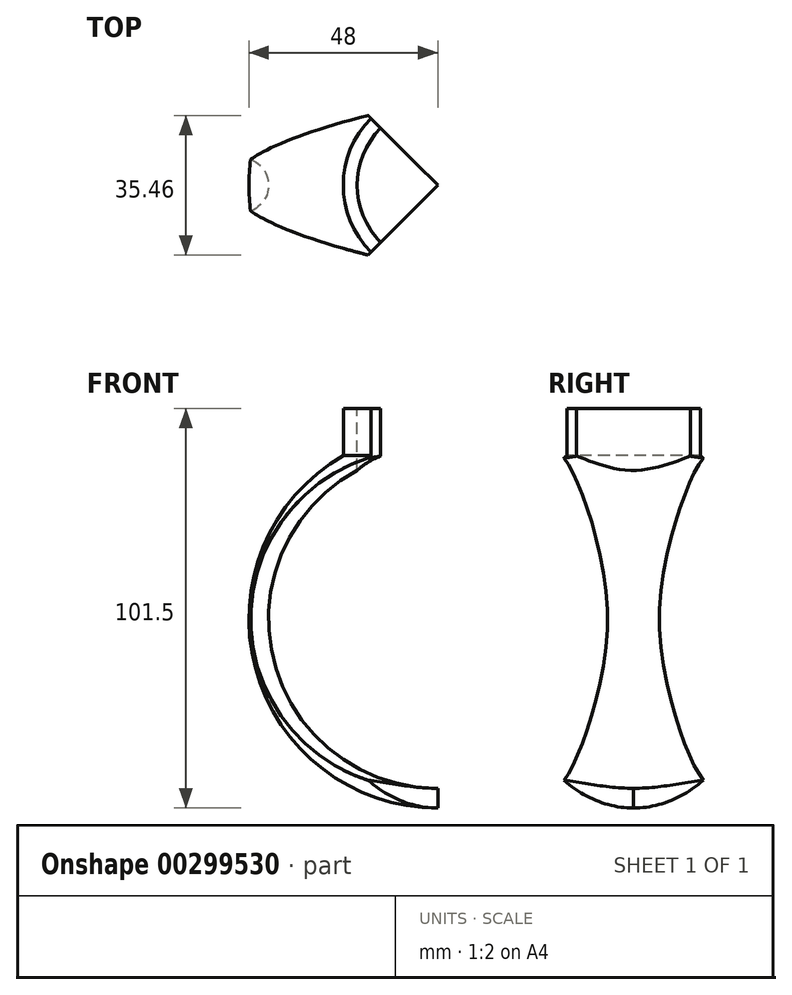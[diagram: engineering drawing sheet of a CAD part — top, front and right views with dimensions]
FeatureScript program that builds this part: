
annotation { "Feature Type Name" : "Feature", "Feature Type Description" : "" }
export const myFeature = defineFeature(function(context is Context, id is Id, definition is map)
    precondition{}
    {
        {
            var Q0;
            Q0=qCreatedBy(makeId("Front.planeOp"),FACE);
            var sketch = newSketch(context, id + "F0", { "sketchPlane" : qUnion([Q0])});
            skLineSegment(sketch, "E0.bottom", {"start": v(0, 75.1) * mm, "end": v(50, 75.1) * mm});
            skLineSegment(sketch, "E0.top", {"start": v(0, -75.3) * mm, "end": v(50, -75.3) * mm});
            skLineSegment(sketch, "E0.left", {"start": v(0, 75.1) * mm, "end": v(0, -75.3) * mm});
            skLineSegment(sketch, "E0.right", {"start": v(50, 75.1) * mm, "end": v(50, -75.3) * mm});
            skArc(sketch, "E1", {"start": v(50, 42.9) * mm, "mid": v(7, -0.1) * mm, "end": v(50, -43.1) * mm});
            skLineSegment(sketch, "E2", {"start": v(0, 53.4) * mm, "end": v(50, 53.4) * mm});
            skLineSegment(sketch, "E3", {"start": v(0, -50.35) * mm, "end": v(50, -50.35) * mm});
            skArc(sketch, "E4", {"start": v(26, 41.47) * mm, "mid": v(3.64, -12.52) * mm, "end": v(50, -48.1) * mm});
            skLineSegment(sketch, "E5", {"start": v(26, 53.4) * mm, "end": v(26, 41.47) * mm});
            skSolve(sketch);
        }
        {
            var Q0;
            {var subQ4=sQuery(id+"F0.wireOp",EDGE,"E1");Q0=makeQuery(id+"F0.imprint","IMPRINT",FACE,{"disambiguationData":[TD([[makeQuery(id+"F0.imprint","IMPRINT",EDGE,{"derivedFrom":subQ4}),-1.0]])]});}
            var Q1;
            Q1=sQuery(id+"F0.wireOp",EDGE,"E0.right");
            revolve(context, id + "F1", {"surfaceOperationType" : NewSurfaceOperationType.NEW, "entities" : qUnion([Q0]), "axis" : qUnion([Q1]), "revolveType" : RevolveType.SYMMETRIC, "angle" : 90 * degree});
        }
        {
            var Q0;
            {var subQ0=sQuery(id+"F0.wireOp",EDGE,"E1");Q0=makeQuery(id+"F0.imprint","IMPRINT",FACE,{"disambiguationData":[TD([[makeQuery(id+"F0.imprint","IMPRINT",EDGE,{"derivedFrom":subQ0}),1.0]])]});}
            var Q1;
            Q1=sQuery(id+"F0.wireOp",EDGE,"E0.left");
            revolve(context, id + "F2", {"operationType" : NewBodyOperationType.REMOVE, "surfaceOperationType" : NewSurfaceOperationType.NEW, "entities" : qUnion([Q0]), "axis" : qUnion([Q1]), "revolveType" : RevolveType.SYMMETRIC, "angle" : 180 * degree});
        }
        {
            var Q0;
            Q0=makeQuery(id+"F1.opRevolve","SWEPT_FACE",FACE,{"disambiguationData":[OSD([sQuery(id+"F0.wireOp",EDGE,"E2")])]});
            var sketch = newSketch(context, id + "F3", { "sketchPlane" : qUnion([Q0])});
            skCircle(sketch, "E6", {"center": v(50, 0) * mm, "radius": 20.5 * mm});
            skLineSegment(sketch, "E7.bottom", {"start": v(50, 0) * mm, "end": v(21.21, 28.79) * mm});
            skLineSegment(sketch, "E7.top", {"start": v(20.87, -29.13) * mm, "end": v(-7.92, -0.34) * mm});
            skLineSegment(sketch, "E7.left", {"start": v(50, 0) * mm, "end": v(20.87, -29.13) * mm});
            skLineSegment(sketch, "E7.right", {"start": v(21.21, 28.79) * mm, "end": v(-7.92, -0.34) * mm});
            skSolve(sketch);
        }
        {
            var Q0;
            {var subQ0=sQuery(id+"F3.wireOp",EDGE,"E6");var subQ1=sQuery(id+"F0.wireOp",EDGE,"E2");var subQ2=makeQuery(id+"F1.opRevolve","CAP_EDGE",EDGE,{"disambiguationData":[OSD([subQ1])],"isStart":true});var subQ3=makeQuery(id+"F3.imprint","INTERSECT",VERTEX,{"derivedFrom":[subQ2,subQ0]});Q0=makeQuery(id+"F3.imprint","IMPRINT",FACE,{"disambiguationData":[TD([[makeQuery(id+"F3.imprint","IMPRINT",EDGE,{"disambiguationData":[TD([[subQ3,1.0]])],"derivedFrom":subQ0}),1.0]])]});}
            extrude(context, id + "F4", {"entities" : qUnion([Q0]), "operationType" : NewBodyOperationType.REMOVE, "oppositeDirection" : true, "depth" : 25 * mm, "offsetDistance" : 25 * mm});
        }
    });
